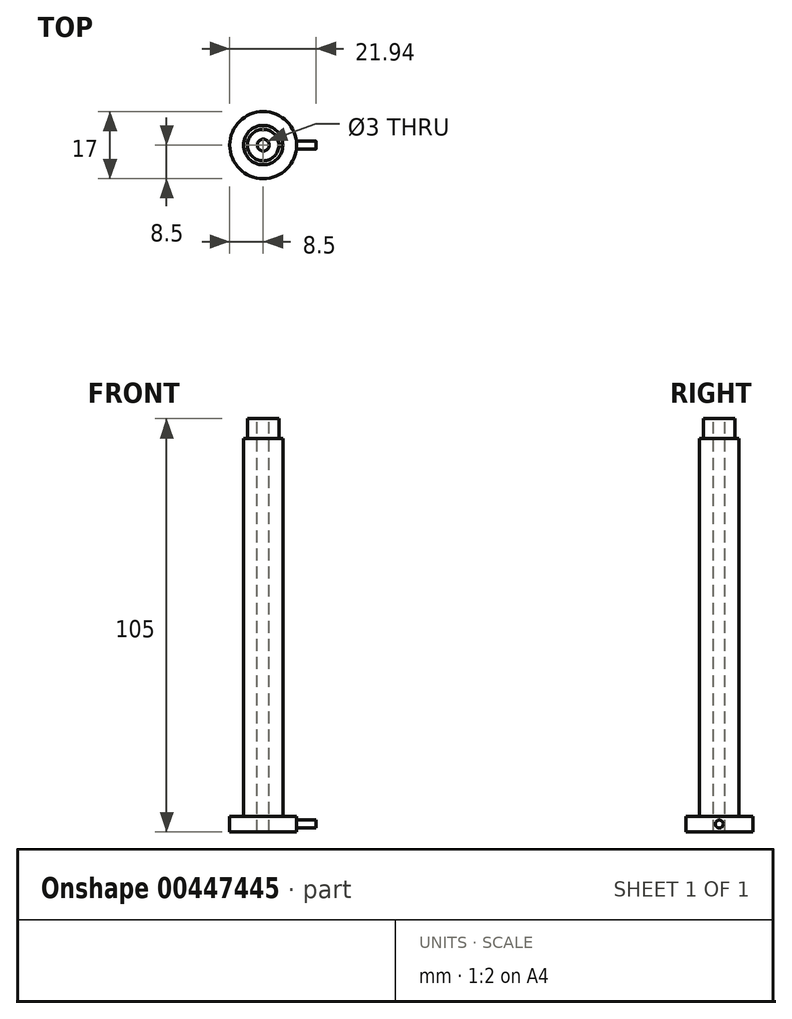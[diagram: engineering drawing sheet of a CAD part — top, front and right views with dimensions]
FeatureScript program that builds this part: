
annotation { "Feature Type Name" : "Feature", "Feature Type Description" : "" }
export const myFeature = defineFeature(function(context is Context, id is Id, definition is map)
    precondition{}
    {
        {
            var Q0;
            Q0=qCreatedBy(makeId("Top.planeOp"),FACE);
            var sketch = newSketch(context, id + "F0", { "sketchPlane" : qUnion([Q0])});
            skCircle(sketch, "E0", {"center": v(0, 0) * mm, "radius": 8.5 * mm});
            skSolve(sketch);
        }
        {
            var Q0;
            Q0=qSketchRegion(id+"F0",true);
            extrude(context, id + "F1", {"entities" : qUnion([Q0]), "depth" : 4 * mm});
        }
        {
            var Q0;
            Q0=qCreatedBy(makeId("Top.planeOp"),FACE);
            cPlane(context, id + "F2", {"entities" : qUnion([Q0]), "cplaneType" : CPlaneType.OFFSET, "offset" : 4 * mm, "width" : 150 * mm, "height" : 150 * mm});
        }
        {
            var Q0;
            Q0=qCreatedBy(makeId("Top.planeOp"),FACE);
            var sketch = newSketch(context, id + "F3", { "sketchPlane" : qUnion([Q0])});
            skCircle(sketch, "E1", {"center": v(0, 0) * mm, "radius": 5 * mm});
            skSolve(sketch);
        }
        {
            var Q0;
            Q0=qSketchRegion(id+"F3",true);
            extrude(context, id + "F4", {"entities" : qUnion([Q0]), "operationType" : NewBodyOperationType.ADD, "depth" : 100 * mm});
        }
        {
            var Q0;
            Q0=qCreatedBy(makeId("Right.planeOp"),FACE);
            var sketch = newSketch(context, id + "F5", { "sketchPlane" : qUnion([Q0])});
            skLineSegment(sketch, "E2.bottom", {"start": v(0, 105) * mm, "end": v(4, 105) * mm});
            skLineSegment(sketch, "E2.top", {"start": v(0, 100) * mm, "end": v(4, 100) * mm});
            skLineSegment(sketch, "E2.left", {"start": v(0, 105) * mm, "end": v(0, 100) * mm});
            skLineSegment(sketch, "E2.right", {"start": v(4, 105) * mm, "end": v(4, 100) * mm});
            skSolve(sketch);
        }
        {
            var Q0;
            Q0=makeQuery(id+"F5.imprint","IMPRINT",FACE,{"disambiguationData":[TD([[makeQuery(id+"F5.imprint","IMPRINT",EDGE,{"derivedFrom":sQuery(id+"F5.wireOp",EDGE,"E2.bottom")}),-1.0]])]});
            var Q1;
            Q1=sQuery(id+"F5.wireOp",EDGE,"E2.left");
            revolve(context, id + "F6", {"operationType" : NewBodyOperationType.ADD, "entities" : qUnion([Q0]), "axis" : qUnion([Q1]), "revolveType" : RevolveType.FULL});
        }
        {
            var Q0;
            Q0=qCreatedBy(id+"F2.planeOp",FACE);
            var sketch = newSketch(context, id + "F7", { "sketchPlane" : qUnion([Q0])});
            skLineSegment(sketch, "E3", {"start": v(8.44, 1) * mm, "end": v(8.44, -1) * mm});
            skSolve(sketch);
        }
        {
            var Q0;
            Q0=sQuery(id+"F7.wireOp",EDGE,"E3");
            cPlane(context, id + "F8", {"entities" : qUnion([Q0]), "cplaneType" : CPlaneType.LINE_ANGLE, "offset" : 25 * mm, "angle" : 90 * degree, "width" : 150 * mm, "height" : 150 * mm});
        }
        {
            var Q0;
            Q0=qCreatedBy(id+"F8.planeOp",FACE);
            var sketch = newSketch(context, id + "F9", { "sketchPlane" : qUnion([Q0])});
            skCircle(sketch, "E4", {"center": v(0, 2) * mm, "radius": 1 * mm});
            skSolve(sketch);
        }
        {
            var Q0;
            Q0=makeQuery(id+"F9.imprint","IMPRINT",FACE,{"disambiguationData":[TD([[makeQuery(id+"F9.imprint","IMPRINT",EDGE,{"derivedFrom":sQuery(id+"F9.wireOp",EDGE,"E4")}),1.0]])]});
            extrude(context, id + "F10", {"entities" : qUnion([Q0]), "operationType" : NewBodyOperationType.ADD, "depth" : 5 * mm});
        }
        {
            var Q0;
            Q0=makeQuery(id+"F6.opRevolve","SWEPT_FACE",FACE,{"disambiguationData":[OSD([sQuery(id+"F5.wireOp",EDGE,"E2.bottom")])]});
            var sketch = newSketch(context, id + "F11", { "sketchPlane" : qUnion([Q0])});
            skCircle(sketch, "E5", {"center": v(0, 0) * mm, "radius": 1.5 * mm});
            skSolve(sketch);
        }
        {
            var Q0;
            Q0 = qSketchRegion(id + "F11", true);
            extrude(context, id + "F12", {"entities" : qUnion([Q0]), "operationType" : NewBodyOperationType.REMOVE, "oppositeDirection" : true, "depth" : 128.4 * mm});
        }
    });
